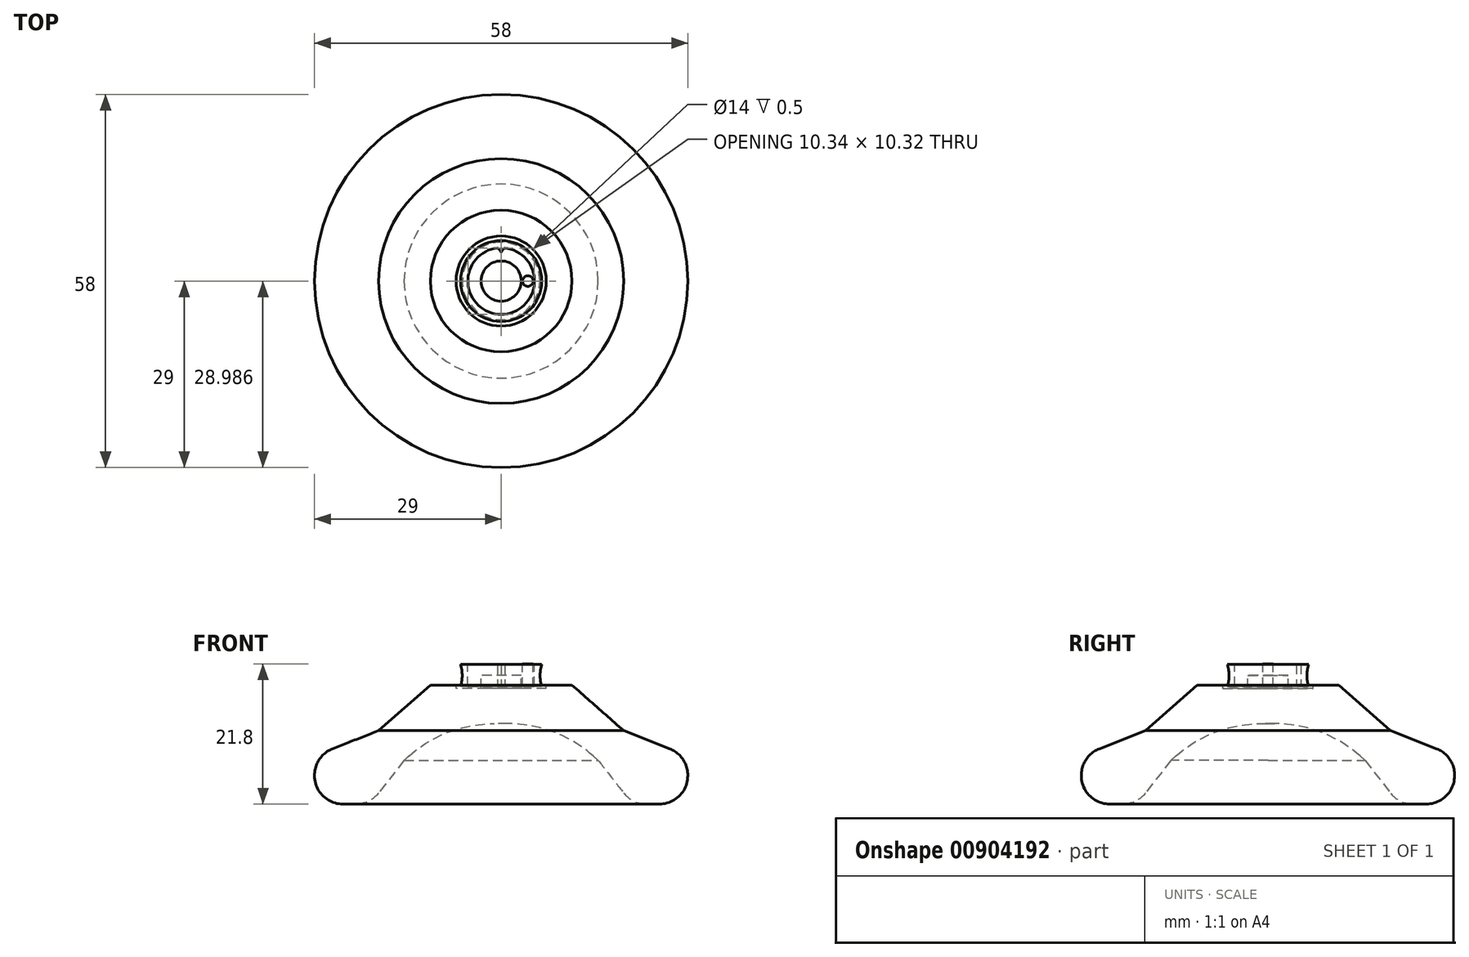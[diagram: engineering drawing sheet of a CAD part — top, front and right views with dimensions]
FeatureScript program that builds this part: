
annotation { "Feature Type Name" : "Feature", "Feature Type Description" : "" }
export const myFeature = defineFeature(function(context is Context, id is Id, definition is map)
    precondition{}
    {
        {
            var Q0;
            Q0=qCreatedBy(makeId("Front.planeOp"),FACE);
            var sketch = newSketch(context, id + "F0", { "sketchPlane" : qUnion([Q0])});
            skLineSegment(sketch, "E0", {"start": v(0, 0) * mm, "end": v(0, -7.5) * mm});
            skLineSegment(sketch, "E1", {"start": v(0, 0) * mm, "end": v(37.55, 0) * mm, "construction": true});
            skLineSegment(sketch, "E2", {"start": v(20.38, -20) * mm, "end": v(29, -20) * mm});
            skLineSegment(sketch, "E3", {"start": v(29, -20) * mm, "end": v(29, -12.5) * mm});
            skLineSegment(sketch, "E4", {"start": v(11, -1.5) * mm, "end": v(7, -1.5) * mm});
            skLineSegment(sketch, "E5", {"start": v(7, -1.5) * mm, "end": v(7, -2) * mm});
            skLineSegment(sketch, "E6", {"start": v(7, -2) * mm, "end": v(3.12, -2) * mm});
            skLineSegment(sketch, "E7", {"start": v(3.12, -2) * mm, "end": v(3.12, 0) * mm});
            skLineSegment(sketch, "E8", {"start": v(3.12, 0) * mm, "end": v(0, 0) * mm});
            skLineSegment(sketch, "E9", {"start": v(11, -1.5) * mm, "end": v(19.03, -8.59) * mm});
            skLineSegment(sketch, "E10", {"start": v(19.03, -8.59) * mm, "end": v(29, -12.5) * mm});
            skLineSegment(sketch, "E11", {"start": v(0, -7.5) * mm, "end": v(8.62, -7.5) * mm});
            skLineSegment(sketch, "E12", {"start": v(8.62, -7.5) * mm, "end": v(15.08, -13.2) * mm});
            skLineSegment(sketch, "E13", {"start": v(15.08, -13.2) * mm, "end": v(20.38, -20) * mm});
            skSolve(sketch);
        }
        {
            var Q0;
            Q0=makeQuery(id+"F0.imprint","IMPRINT",FACE,{"disambiguationData":[TD([[makeQuery(id+"F0.imprint","IMPRINT",EDGE,{"derivedFrom":sQuery(id+"F0.wireOp",EDGE,"E0")}),1.0]])]});
            var Q1;
            Q1=sQuery(id+"F0.wireOp",EDGE,"E0");
            revolve(context, id + "F1", {"surfaceOperationType" : NewSurfaceOperationType.NEW, "entities" : qUnion([Q0]), "axis" : qUnion([Q1]), "revolveType" : RevolveType.FULL});
        }
        {
            var Q0;
            Q0=makeQuery(id+"F1.opRevolve","SWEPT_EDGE",EDGE,{"disambiguationData":[OSD([sQuery(id+"F0.wireOp",EDGE,"E3"),sQuery(id+"F0.wireOp",EDGE,"E10")])]});
            var Q1;
            Q1=makeQuery(id+"F1.opRevolve","SWEPT_EDGE",EDGE,{"disambiguationData":[OSD([sQuery(id+"F0.wireOp",EDGE,"E2"),sQuery(id+"F0.wireOp",EDGE,"E3")])]});
            var Q2;
            Q2=makeQuery(id+"F1.opRevolve","SWEPT_EDGE",EDGE,{"disambiguationData":[OSD([sQuery(id+"F0.wireOp",EDGE,"E2"),sQuery(id+"F0.wireOp",EDGE,"E13")])]});
            fillet(context, id + "F2", {"entities" : qUnion([Q0, Q1, Q2]), "radius" : 4.4 * mm, "tangentPropagation" : true, "allowEdgeOverflow" : false});
        }
        {
            var Q0;
            Q0=makeQuery(id+"F1.opRevolve","SWEPT_EDGE",EDGE,{"disambiguationData":[OSD([sQuery(id+"F0.wireOp",EDGE,"E11"),sQuery(id+"F0.wireOp",EDGE,"E12")])]});
            fillet(context, id + "F3", {"entities" : qUnion([Q0]), "radius" : 20 * mm, "tangentPropagation" : true, "allowEdgeOverflow" : false});
        }
        {
            var Q0;
            Q0=qCreatedBy(makeId("Front.planeOp"),FACE);
            var sketch = newSketch(context, id + "F4", { "sketchPlane" : qUnion([Q0])});
            skLineSegment(sketch, "E14", {"start": v(0, 3.53) * mm, "end": v(0, -3.93) * mm, "construction": true});
            skLineSegment(sketch, "E15.bottom", {"start": v(3.33, 1.8) * mm, "end": v(4.15, 1.8) * mm});
            skLineSegment(sketch, "E15.top", {"start": v(3.33, -1.8) * mm, "end": v(4.15, -1.8) * mm});
            skLineSegment(sketch, "E15.left", {"start": v(3.33, 1.8) * mm, "end": v(3.33, -1.8) * mm});
            skLineSegment(sketch, "E15.right", {"start": v(4.15, 1.8) * mm, "end": v(4.15, -1.8) * mm});
            skLineSegment(sketch, "E16.bottom", {"start": v(5.18, 1.7) * mm, "end": v(6.3, 1.7) * mm});
            skLineSegment(sketch, "E16.top", {"start": v(5.18, -1.7) * mm, "end": v(6.3, -1.7) * mm});
            skLineSegment(sketch, "E16.left", {"start": v(5.18, 1.7) * mm, "end": v(5.18, -1.7) * mm});
            skPoint(sketch, "E17", {"position": v(5.18, 0) * mm});
            skPoint(sketch, "E18", {"position": v(3.33, 0) * mm});
            skArc(sketch, "E19", {"start": v(6.3, 1.7) * mm, "mid": v(6.05, 0) * mm, "end": v(6.3, -1.7) * mm});
            skPoint(sketch, "E19.centerSnap0", {"position": v(6.4, 0) * mm});
            skSolve(sketch);
        }
        {
            var Q0;
            Q0=makeQuery(id+"F4.imprint","IMPRINT",FACE,{"disambiguationData":[TD([[makeQuery(id+"F4.imprint","IMPRINT",EDGE,{"derivedFrom":sQuery(id+"F4.wireOp",EDGE,"E16.bottom")}),-1.0]])]});
            var Q1;
            Q1=sQuery(id+"F4.wireOp",EDGE,"E14");
            revolve(context, id + "F5", {"surfaceOperationType" : NewSurfaceOperationType.NEW, "entities" : qUnion([Q0]), "axis" : qUnion([Q1]), "revolveType" : RevolveType.FULL});
        }
        {
            var Q0;
            Q0=makeQuery(id+"F4.imprint","IMPRINT",FACE,{"disambiguationData":[TD([[makeQuery(id+"F4.imprint","IMPRINT",EDGE,{"derivedFrom":sQuery(id+"F4.wireOp",EDGE,"E15.bottom")}),-1.0]])]});
            var Q1;
            Q1=sQuery(id+"F4.wireOp",EDGE,"E15.right");
            revolve(context, id + "F6", {"surfaceOperationType" : NewSurfaceOperationType.NEW, "entities" : qUnion([Q0]), "axis" : qUnion([Q1]), "revolveType" : RevolveType.FULL});
        }
        {
            var Q0;
            Q0=qCreatedBy(makeId("Top.planeOp"),FACE);
            var sketch = newSketch(context, id + "F7", { "sketchPlane" : qUnion([Q0])});
            skArc(sketch, "E20", {"start": v(0.68, 5.26) * mm, "mid": v(0, 5.3) * mm, "end": v(-0.68, 5.26) * mm});
            skArc(sketch, "E21", {"start": v(0, 4.44) * mm, "mid": v(-0.3, 4.9) * mm, "end": v(-0.68, 5.26) * mm});
            skArc(sketch, "E22", {"start": v(0.68, 5.26) * mm, "mid": v(0.3, 4.9) * mm, "end": v(0, 4.44) * mm});
            skLineSegment(sketch, "E23", {"start": v(0, 0) * mm, "end": v(-2, 3.46) * mm, "construction": true});
            skLineSegment(sketch, "E24", {"start": v(2, 3.46) * mm, "end": v(-2, 3.46) * mm, "construction": true});
            skLineSegment(sketch, "E25", {"start": v(0, 0) * mm, "end": v(2, 3.46) * mm, "construction": true});
            skSolve(sketch);
        }
        {
            var Q0;
            Q0 = qSketchRegion(id + "F7", true);
            extrude(context, id + "F8", {"entities" : qUnion([Q0]), "operationType" : NewBodyOperationType.ADD, "depth" : 3.4 * mm, "offsetDistance" : 25 * mm, "symmetric" : true});
        }
    });
